# Revit family: QF_Gemüseschneider Varimat Speed
name_source: partatom
category: Sonderausstattung
units: mm (PartAtom-declared; Revit-internal decimal feet)

## family parameters
Arbeitsebenenbasiert = Nein
Beim Laden mit Abzugskörper schneiden = Nein
Bemaßung runder Anschluss = Durchmesser verwenden
Gemeinsam genutzt = Nein
Immer vertikal = Ja
OmniClass-Nummer = 23.40.40.14.14
OmniClass-Titel = Food Preparation Equipment
Raumberechnungspunkt = Nein
Teiletyp = Normal

## types (1)
- Varimat Speed
    Beschreibung = Gemüseschneider
    Beschreibung durch Hersteller analog Leistungsverzeichnislangtext = Maschinenbasisversion mit Edelstahlgehäuse 
und komplett abnehmbaren  
Edelstahl- Gemüseschneidvorsatz Varimat GD, 
hygienische Reinigung in der Spülmaschine, 
Sicherheitsabschaltung und Abschaltautomatik,  

Geschwindigkeit variabel 150-750 U/min,
starker durchzugskräftiger Markenmotor 
mit Getriebe und Motorschutzschalter,
erweiterbar mit Deckel des Gourmetvorsatzes für Gaufrettes
und Brunoise, GN-Behälter mit Höhe 200 mm und Höhe 250 mm unterstellbar

schlagfeste Schalter,
stromsparend mit Hauptschalter,
CE-geprüft
GS-zertifiziert
IP65-Zertifikat
    Elektrische Leistung = 400 W
    Frequenz = 50 Hz
    Garantiezeit = 24 Monate
    Gerätegewicht Netto = 21,00 kg
    Hauptschalter integriert = Ja
    Hersteller = Rotor Lips AG
    Höhe = 526 mm  [stored 1.72572 ft]
    IP Schutzart = IP65-Zertifikat
    Internetadresse Gerätehersteller = www.rotorlips.ch
    Internetadresse für Ersatzteilliste = www.rotorlips.ch
    Länge Gerätebreite = 261 mm
    Material = Edelstahl
    Modell = Varimat Speed
    Phasen = 1
    Spannung = 230 V
    Tiefe = 508 mm
    Typenkommentare = Freistehendes, universell einsetzbarer Gemüseschneider für: klassische Scheibenanwendungen sowie Würfeln und Spezialschnitte wie Brunoise (kleine Würfel) und Gaufrettes (Waffelschnitt/gekreuzter Wellenschnitt)
    URL = www.rotorlips.ch

note: [stored X ft] marks values corroborated as IEEE doubles in the binary element streams (Revit-internal decimal feet)
